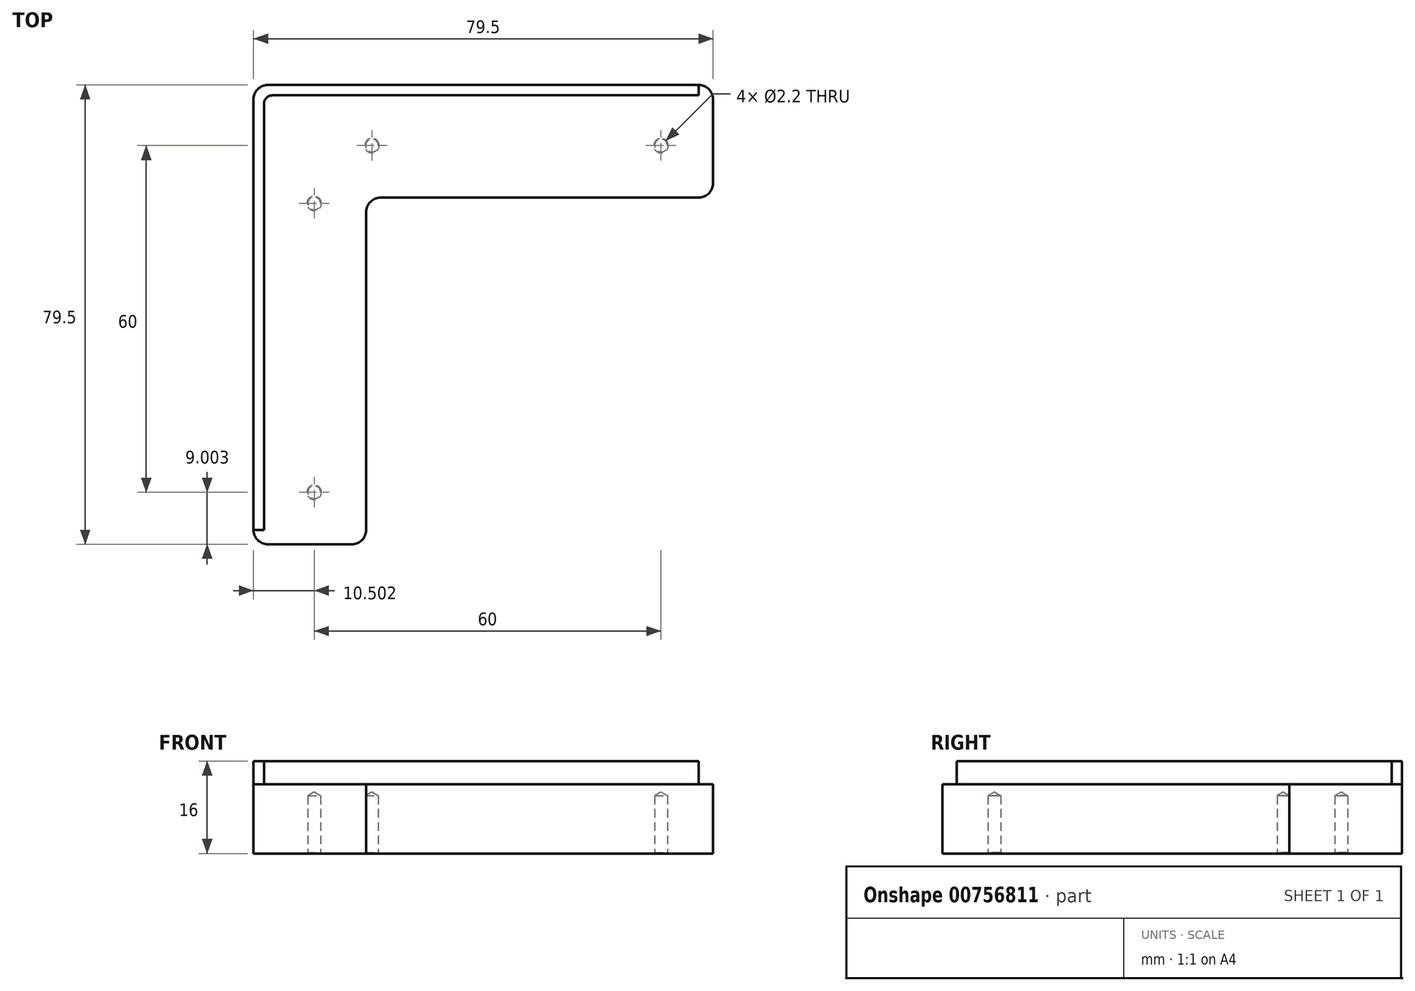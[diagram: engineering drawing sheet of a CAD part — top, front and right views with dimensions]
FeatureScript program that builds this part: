
annotation { "Feature Type Name" : "Feature", "Feature Type Description" : "" }
export const myFeature = defineFeature(function(context is Context, id is Id, definition is map)
    precondition{}
    {
        {
            var Q0;
            Q0=qCreatedBy(makeId("Top.planeOp"),FACE);
            var sketch = newSketch(context, id + "F0", { "sketchPlane" : qUnion([Q0])});
            skLineSegment(sketch, "E0", {"start": v(-33.29, 36.54) * mm, "end": v(41.21, 36.54) * mm});
            skLineSegment(sketch, "E1", {"start": v(43.71, 34.04) * mm, "end": v(43.71, 19.54) * mm});
            skLineSegment(sketch, "E2", {"start": v(41.21, 17.04) * mm, "end": v(-13.79, 17.04) * mm});
            skLineSegment(sketch, "E3", {"start": v(-16.29, 14.54) * mm, "end": v(-16.29, -40.46) * mm});
            skLineSegment(sketch, "E4", {"start": v(-18.79, -42.96) * mm, "end": v(-33.29, -42.96) * mm});
            skLineSegment(sketch, "E5", {"start": v(-35.79, -40.46) * mm, "end": v(-35.79, 34.04) * mm});
            skPoint(sketch, "E6.visualSharp", {"position": v(-35.79, 36.54) * mm});
            skArc(sketch, "E6.filletArc", {"start": v(-33.29, 36.54) * mm, "mid": v(-35.06, 35.81) * mm, "end": v(-35.79, 34.04) * mm});
            skPoint(sketch, "E7.visualSharp", {"position": v(43.71, 36.54) * mm});
            skArc(sketch, "E7.filletArc", {"start": v(43.71, 34.04) * mm, "mid": v(42.98, 35.81) * mm, "end": v(41.21, 36.54) * mm});
            skPoint(sketch, "E8.visualSharp", {"position": v(43.71, 17.04) * mm});
            skArc(sketch, "E8.filletArc", {"start": v(41.21, 17.04) * mm, "mid": v(42.98, 17.78) * mm, "end": v(43.71, 19.54) * mm});
            skPoint(sketch, "E9.visualSharp", {"position": v(-16.29, 17.04) * mm});
            skArc(sketch, "E9.filletArc", {"start": v(-13.79, 17.04) * mm, "mid": v(-15.56, 16.31) * mm, "end": v(-16.29, 14.54) * mm});
            skPoint(sketch, "E10.visualSharp", {"position": v(-35.79, -42.96) * mm});
            skArc(sketch, "E10.filletArc", {"start": v(-35.79, -40.46) * mm, "mid": v(-35.06, -42.22) * mm, "end": v(-33.29, -42.96) * mm});
            skPoint(sketch, "E11.visualSharp", {"position": v(-16.29, -42.96) * mm});
            skArc(sketch, "E11.filletArc", {"start": v(-18.79, -42.96) * mm, "mid": v(-17.02, -42.22) * mm, "end": v(-16.29, -40.46) * mm});
            skSolve(sketch);
        }
        {
            var Q0;
            Q0 = qSketchRegion(id + "F0", true);
            extrude(context, id + "F1", {"entities" : qUnion([Q0]), "depth" : 12 * mm, "offsetDistance" : 25 * mm});
        }
        {
            var Q0;
            Q0=makeQuery(id+"F1.opExtrude","CAP_FACE",FACE,{"disambiguationData":[OSD([sQuery(id+"F0.wireOp",EDGE,"E0"),sQuery(id+"F0.wireOp",EDGE,"E1"),sQuery(id+"F0.wireOp",EDGE,"E2"),sQuery(id+"F0.wireOp",EDGE,"E3"),sQuery(id+"F0.wireOp",EDGE,"E4"),sQuery(id+"F0.wireOp",EDGE,"E5"),sQuery(id+"F0.wireOp",EDGE,"E6.filletArc"),sQuery(id+"F0.wireOp",EDGE,"E7.filletArc"),sQuery(id+"F0.wireOp",EDGE,"E8.filletArc"),sQuery(id+"F0.wireOp",EDGE,"E9.filletArc"),sQuery(id+"F0.wireOp",EDGE,"E10.filletArc"),sQuery(id+"F0.wireOp",EDGE,"E11.filletArc")])],"isStart":false});
            var sketch = newSketch(context, id + "F2", { "sketchPlane" : qUnion([Q0])});
            skLineSegment(sketch, "E12.0", {"start": v(-32.49, 34.74) * mm, "end": v(41.21, 34.74) * mm});
            skLineSegment(sketch, "E13.0", {"start": v(-33.99, -40.46) * mm, "end": v(-33.99, 33.24) * mm});
            skArc(sketch, "E14.filletArc", {"start": v(-32.49, 34.74) * mm, "mid": v(-33.55, 34.3) * mm, "end": v(-33.99, 33.24) * mm});
            skLineSegment(sketch, "E15", {"start": v(-33.99, -40.46) * mm, "end": v(-35.79, -40.46) * mm});
            skLineSegment(sketch, "E16", {"start": v(41.21, 34.74) * mm, "end": v(41.21, 36.54) * mm});
            skSolve(sketch);
        }
        {
            var Q0;
            Q0=makeQuery(id+"F2.imprint","IMPRINT",FACE,{"disambiguationData":[TD([[makeQuery(id+"F2.imprint","IMPRINT",EDGE,{"derivedFrom":sQuery(id+"F2.wireOp",EDGE,"E12.0")}),1.0]])]});
            extrude(context, id + "F3", {"entities" : qUnion([Q0]), "operationType" : NewBodyOperationType.ADD, "depth" : 4 * mm, "offsetDistance" : 25 * mm});
        }
        {
            var Q0;
            Q0=makeQuery(id+"F1.opExtrude","CAP_FACE",FACE,{"disambiguationData":[OSD([sQuery(id+"F0.wireOp",EDGE,"E0"),sQuery(id+"F0.wireOp",EDGE,"E1"),sQuery(id+"F0.wireOp",EDGE,"E2"),sQuery(id+"F0.wireOp",EDGE,"E3"),sQuery(id+"F0.wireOp",EDGE,"E4"),sQuery(id+"F0.wireOp",EDGE,"E5"),sQuery(id+"F0.wireOp",EDGE,"E6.filletArc"),sQuery(id+"F0.wireOp",EDGE,"E7.filletArc"),sQuery(id+"F0.wireOp",EDGE,"E8.filletArc"),sQuery(id+"F0.wireOp",EDGE,"E9.filletArc"),sQuery(id+"F0.wireOp",EDGE,"E10.filletArc"),sQuery(id+"F0.wireOp",EDGE,"E11.filletArc")])],"isStart":true});
            var sketch = newSketch(context, id + "F4", { "sketchPlane" : qUnion([Q0])});
            skLineSegment(sketch, "E17.0", {"start": v(-33.29, -26.04) * mm, "end": v(41.21, -26.04) * mm, "construction": true});
            skLineSegment(sketch, "E18.0", {"start": v(-25.29, 40.46) * mm, "end": v(-25.29, -31.54) * mm, "construction": true});
            skLineSegment(sketch, "E19.0", {"start": v(-18.79, 33.96) * mm, "end": v(-33.29, 33.96) * mm, "construction": true});
            skLineSegment(sketch, "E20.0", {"start": v(34.71, -31.54) * mm, "end": v(34.71, -17.04) * mm, "construction": true});
            skLineSegment(sketch, "E21.0", {"start": v(-18.79, -16.04) * mm, "end": v(-33.29, -16.04) * mm, "construction": true});
            skLineSegment(sketch, "E22.0", {"start": v(-15.29, -31.54) * mm, "end": v(-15.29, -17.04) * mm, "construction": true});
            skPoint(sketch, "E23", {"position": v(34.71, -26.04) * mm});
            skPoint(sketch, "E24", {"position": v(-15.29, -26.04) * mm});
            skPoint(sketch, "E25", {"position": v(-25.29, -16.04) * mm});
            skPoint(sketch, "E26", {"position": v(-25.29, 33.96) * mm});
            skSolve(sketch);
        }
        {
            var Q0;
            Q0=sQuery(id+"F4.wireOp",VERTEX,"E23");
            var Q1;
            Q1=makeQuery(id+"F1.opExtrude","SWEPT_BODY",BODY,{"disambiguationData":[OSD([sQuery(id+"F0.wireOp",EDGE,"E0"),sQuery(id+"F0.wireOp",EDGE,"E1"),sQuery(id+"F0.wireOp",EDGE,"E2"),sQuery(id+"F0.wireOp",EDGE,"E3"),sQuery(id+"F0.wireOp",EDGE,"E4"),sQuery(id+"F0.wireOp",EDGE,"E5"),sQuery(id+"F0.wireOp",EDGE,"E6.filletArc"),sQuery(id+"F0.wireOp",EDGE,"E7.filletArc"),sQuery(id+"F0.wireOp",EDGE,"E8.filletArc"),sQuery(id+"F0.wireOp",EDGE,"E9.filletArc"),sQuery(id+"F0.wireOp",EDGE,"E10.filletArc"),sQuery(id+"F0.wireOp",EDGE,"E11.filletArc")])]});
            hole(context, id + "F5", {"style" : HoleStyle.C_SINK, "endStyle" : HoleEndStyle.BLIND, "holeDiameter" : 2.2 * mm, "cSinkDiameter" : 2.5 * mm, "cSinkAngle" : 90 * degree, "majorDiameter" : 5 * mm, "holeDepth" : 10 * mm, "isTappedThrough" : true, "tappedDepth" : 12 * mm, "tapClearance" : 3, "startFromSketch" : true, "locations" : qUnion([Q0]), "scope" : qUnion([Q1])});
        }
        {
            var Q0;
            Q0=sQuery(id+"F4.wireOp",VERTEX,"E24");
            var Q1;
            Q1=makeQuery(id+"F1.opExtrude","SWEPT_BODY",BODY,{"disambiguationData":[OSD([sQuery(id+"F0.wireOp",EDGE,"E0"),sQuery(id+"F0.wireOp",EDGE,"E1"),sQuery(id+"F0.wireOp",EDGE,"E2"),sQuery(id+"F0.wireOp",EDGE,"E3"),sQuery(id+"F0.wireOp",EDGE,"E4"),sQuery(id+"F0.wireOp",EDGE,"E5"),sQuery(id+"F0.wireOp",EDGE,"E6.filletArc"),sQuery(id+"F0.wireOp",EDGE,"E7.filletArc"),sQuery(id+"F0.wireOp",EDGE,"E8.filletArc"),sQuery(id+"F0.wireOp",EDGE,"E9.filletArc"),sQuery(id+"F0.wireOp",EDGE,"E10.filletArc"),sQuery(id+"F0.wireOp",EDGE,"E11.filletArc")])]});
            hole(context, id + "F6", {"style" : HoleStyle.C_SINK, "endStyle" : HoleEndStyle.BLIND, "holeDiameter" : 2.2 * mm, "cSinkDiameter" : 2.5 * mm, "cSinkAngle" : 90 * degree, "majorDiameter" : 5 * mm, "holeDepth" : 10 * mm, "isTappedThrough" : true, "tappedDepth" : 12 * mm, "tapClearance" : 3, "startFromSketch" : true, "locations" : qUnion([Q0]), "scope" : qUnion([Q1])});
        }
        {
            var Q0;
            Q0=sQuery(id+"F4.wireOp",VERTEX,"E25");
            var Q1;
            Q1=makeQuery(id+"F1.opExtrude","SWEPT_BODY",BODY,{"disambiguationData":[OSD([sQuery(id+"F0.wireOp",EDGE,"E0"),sQuery(id+"F0.wireOp",EDGE,"E1"),sQuery(id+"F0.wireOp",EDGE,"E2"),sQuery(id+"F0.wireOp",EDGE,"E3"),sQuery(id+"F0.wireOp",EDGE,"E4"),sQuery(id+"F0.wireOp",EDGE,"E5"),sQuery(id+"F0.wireOp",EDGE,"E6.filletArc"),sQuery(id+"F0.wireOp",EDGE,"E7.filletArc"),sQuery(id+"F0.wireOp",EDGE,"E8.filletArc"),sQuery(id+"F0.wireOp",EDGE,"E9.filletArc"),sQuery(id+"F0.wireOp",EDGE,"E10.filletArc"),sQuery(id+"F0.wireOp",EDGE,"E11.filletArc")])]});
            hole(context, id + "F7", {"style" : HoleStyle.C_SINK, "endStyle" : HoleEndStyle.BLIND, "holeDiameter" : 2.2 * mm, "cSinkDiameter" : 2.5 * mm, "cSinkAngle" : 90 * degree, "majorDiameter" : 5 * mm, "holeDepth" : 10 * mm, "isTappedThrough" : true, "tappedDepth" : 12 * mm, "tapClearance" : 3, "startFromSketch" : true, "locations" : qUnion([Q0]), "scope" : qUnion([Q1])});
        }
        {
            var Q0;
            Q0=sQuery(id+"F4.wireOp",VERTEX,"E26");
            var Q1;
            Q1=makeQuery(id+"F1.opExtrude","SWEPT_BODY",BODY,{"disambiguationData":[OSD([sQuery(id+"F0.wireOp",EDGE,"E0"),sQuery(id+"F0.wireOp",EDGE,"E1"),sQuery(id+"F0.wireOp",EDGE,"E2"),sQuery(id+"F0.wireOp",EDGE,"E3"),sQuery(id+"F0.wireOp",EDGE,"E4"),sQuery(id+"F0.wireOp",EDGE,"E5"),sQuery(id+"F0.wireOp",EDGE,"E6.filletArc"),sQuery(id+"F0.wireOp",EDGE,"E7.filletArc"),sQuery(id+"F0.wireOp",EDGE,"E8.filletArc"),sQuery(id+"F0.wireOp",EDGE,"E9.filletArc"),sQuery(id+"F0.wireOp",EDGE,"E10.filletArc"),sQuery(id+"F0.wireOp",EDGE,"E11.filletArc")])]});
            hole(context, id + "F8", {"style" : HoleStyle.C_SINK, "endStyle" : HoleEndStyle.BLIND, "holeDiameter" : 2.2 * mm, "cSinkDiameter" : 2.5 * mm, "cSinkAngle" : 90 * degree, "majorDiameter" : 5 * mm, "holeDepth" : 10 * mm, "isTappedThrough" : true, "tappedDepth" : 12 * mm, "tapClearance" : 3, "startFromSketch" : true, "locations" : qUnion([Q0]), "scope" : qUnion([Q1])});
        }
    });
